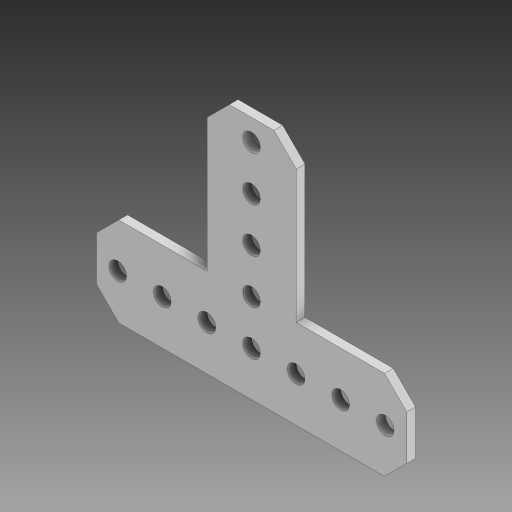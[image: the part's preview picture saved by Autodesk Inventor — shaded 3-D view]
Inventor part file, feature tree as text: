
AUTODESK INVENTOR PART (.ipt)
format: ipt  version: 2023.4 (Build 274418000, 418)  size: 130,048 bytes
history: native  units: in
note: dims shown in document units (in); Inventor stores cm internally (conversion verified against a paired STEP export)
features: chamfer x1
ambient origin geometry x8: Origin, YZ Plane, XZ Plane, XY Plane, X Axis, Y Axis, Z Axis, Center Point
bodies: Solid1 (feature_tree)
feature tree (1):
  chamfer  "Chamfer1"  [1 undecoded]
note: 1 required parameter value undecoded (feature->parameter linkage not recoverable at this tier; creation-order binding heuristic only, values carry confidence <= 0.55)
